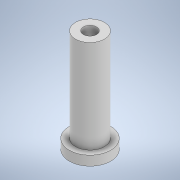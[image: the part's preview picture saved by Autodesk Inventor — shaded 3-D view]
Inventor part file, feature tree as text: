
AUTODESK INVENTOR PART (.ipt)
format: ipt  version: 2021 (Build 250183000, 183)  size: 114,688 bytes
history: native  units: mm
features: revolve x1, sketch x1
ambient origin geometry x8: Origin, YZ Plane, XZ Plane, XY Plane, X Axis, Y Axis, Z Axis, Center Point
bodies: Solid1 (feature_tree)
feature tree (2):
  revolve  "Revolution1"  Angle=90.0deg
  sketch  "Sketch1"  dims[d5=40.4mm d10=90.0deg d12=3.0mm d13=10.0mm d14=3.2mm]
